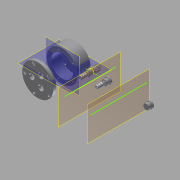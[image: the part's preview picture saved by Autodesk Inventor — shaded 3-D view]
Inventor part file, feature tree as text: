
AUTODESK INVENTOR PART (.ipt)
format: ipt  version: 2012 (Build 160160000, 160)  size: 563,712 bytes
history: native  units: in
note: dims shown in document units (in); Inventor stores cm internally (conversion verified against a paired STEP export)
features: sketch x17, extrude x13, plane x4, revolve x2, mirror x2
ambient origin geometry x8: Origin, YZ Plane, XZ Plane, XY Plane, X Axis, Y Axis, Z Axis, Center Point
bodies: Solid1 (feature_tree)
feature tree (38):
  extrude  "Extrusion1"  Depth=0.3in TaperAngle=0.0deg
  extrude  "Extrusion2"  Depth=0.1135in TaperAngle=0.0deg
  extrude  "Extrusion3"  Depth=0.158in
  plane  "Work Plane1"
  extrude  "Extrusion4"  Depth=0.4in TaperAngle=0.0deg
  extrude  "Extrusion5"  Depth=2.125in
  extrude  "Extrusion6"  Depth=0.25in TaperAngle=0.0deg
  extrude  "Extrusion7"  Depth=0.586in
  sketch  "Sketch8"  dims[d28=1.1811in d30=360.0deg d32=0.4in d33=0.0in]
  plane  "Work Plane2"
  revolve  "Revolution1"  [1 undecoded]
  extrude  "Extrusion8"  Depth=0.53in
  extrude  "Extrusion9"  Depth=0.3in TaperAngle=0.0deg
  revolve  "Revolution2"  [1 undecoded]
  sketch  "Sketch14"  dims[d50=15.0deg d51=0.055in]
  plane  "Work Plane3"
  plane  "Work Plane4"
  mirror  "Mirror1"
  extrude  "Extrusion10"  TaperAngle=90.0deg  [1 undecoded]
  mirror  "Mirror2"
  extrude  "Extrusion11"  Depth=0.055in
  extrude  "Extrusion12"  Depth=0.055in
  extrude  "Extrusion13"  Depth=0.055in
  sketch  "Sketch1"  dims[d0=3.0in d1=0.3in d2=0.0in]
  sketch  "Sketch2"  dims[d6=1.9685in d8=360.0deg d10=0.1135in d11=0.0in]
  sketch  "Sketch3"  dims[d12=1.25in d13=0.158in]
  sketch  "Sketch4"  dims[d14=1.9685in d16=360.0deg d18=0.4in d19=0.0in]
  sketch  "Sketch5"  dims[d20=2.0625in d21=2.125in]
  sketch  "Sketch6"  dims[d22=1.0in d23=0.0in d24=0.25in d25=0.0in]
  sketch  "Sketch7"  dims[d26=0.53in d27=0.586in]
  sketch  "Sketch9"  dims[d34=0.53in d35=0.53in]
  sketch  "Sketch10"  dims[d36=0.23in d37=0.3in d38=0.0in]
  sketch  "Sketch11"  dims[d39=90.0deg d43=0.0in]
  sketch  "Sketch13"  dims[d46=0.15in d49=90.0deg]
  sketch  "Sketch15"  dims[d52=15.0deg d53=0.055in]
  sketch  "Sketch16"  dims[d54=15.0deg d55=0.055in]
  sketch  "Sketch17"  dims[d56=0.055in]
  sketch  "Sketch18"  dims[d57=0.055in d58=0.25in d59=1.0in d60=0.0in d61=0.635in d62=0.15in d63=0.0in d64=0.15in d65=0.18in d66=90.0deg d67=90.0deg d68=90.0deg d69=1.0in d70=0.0in d71=1.0in d72=0.0in d73=0.45in d74=0.0in d75=3.0in d76=0.0in]
note: 3 required parameter values undecoded (feature->parameter linkage not recoverable at this tier; creation-order binding heuristic only, values carry confidence <= 0.55)